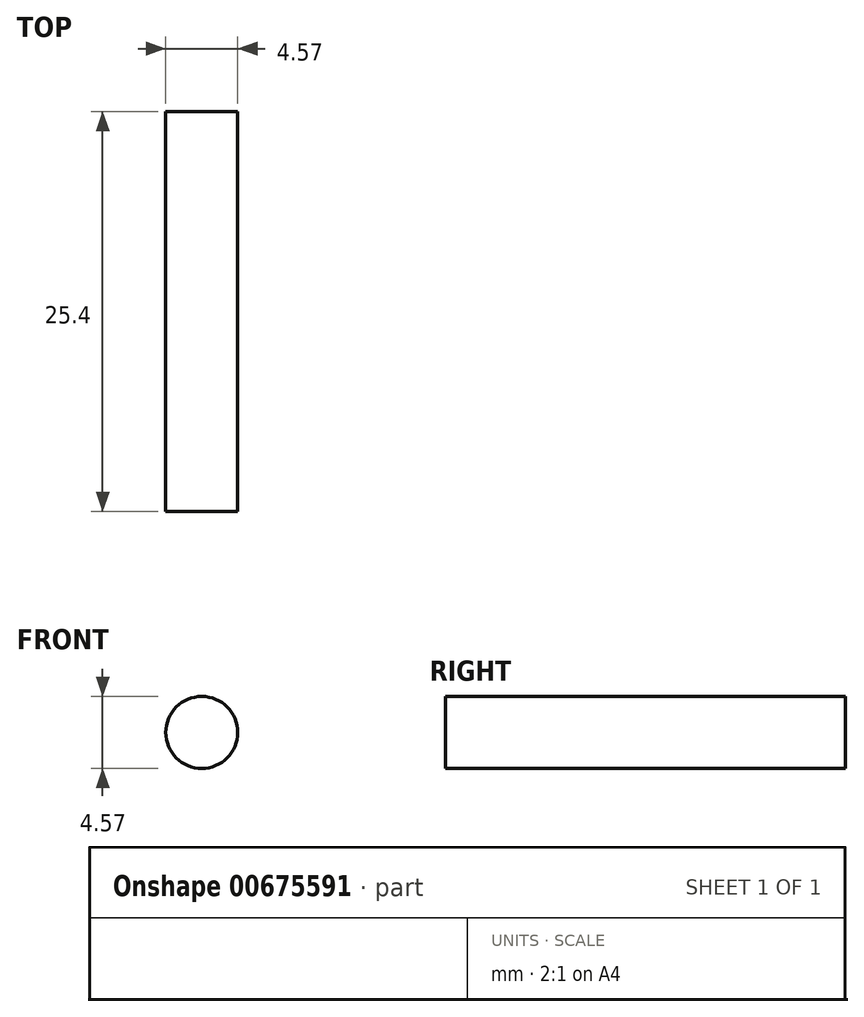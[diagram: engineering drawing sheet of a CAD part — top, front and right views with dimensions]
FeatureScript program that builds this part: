
annotation { "Feature Type Name" : "Feature", "Feature Type Description" : "" }
export const myFeature = defineFeature(function(context is Context, id is Id, definition is map)
    precondition{}
    {
        {
            var Q0;
            Q0=qCreatedBy(makeId("Front.planeOp"),FACE);
            var sketch = newSketch(context, id + "F0", { "sketchPlane" : qUnion([Q0])});
            skCircle(sketch, "E0", {"center": v(-37.33, 25.68) * mm, "radius": 2.29 * mm});
            skSolve(sketch);
        }
        {
            var Q0;
            Q0=makeQuery(id+"F0.imprint","IMPRINT",FACE,{"disambiguationData":[TD([[makeQuery(id+"F0.imprint","IMPRINT",EDGE,{"derivedFrom":sQuery(id+"F0.wireOp",EDGE,"E0")}),1.0]])]});
            extrude(context, id + "F1", {"entities" : qUnion([Q0]), "depth" : 25.4 * mm, "offsetDistance" : 25.4 * mm});
        }
    });
